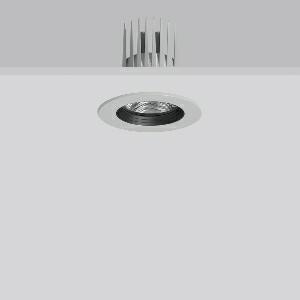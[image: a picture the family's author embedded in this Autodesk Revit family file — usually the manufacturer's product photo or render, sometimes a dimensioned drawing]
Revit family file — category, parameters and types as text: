
# Revit family: heledon_mini_e_901749_004_1_7af7
name_source: partatom
category: Lighting Fixtures
units: mm (PartAtom-declared; Revit-internal decimal feet)

## family parameters
Cut with Voids When Loaded = No
Host = Face
Light Source = No
Part Type = Normal
Room Calculation Point = No
Round Connector Dimension = Use Diameter
Shared = No

## types (1)
- HELEDON mini E (1 x LED Modul 940, 3700 lm, 4000)
    Apparent Load = 29 VA
    Approval mark = CE
    CIE Flux Codes = 99 100 100 100 100
    Color Rendering = 92
    Color Temperature = 4000
    Default Elevation = 1800 mm
    Description = Series: HELEDON mini
Round recessed downlight. Housing: die-cast aluminium, powder-coated. Black plastic ring and recessed LED to prevent glare from the side. Optical assembly with reflector made of MIRO-Silver with 98% total light reflection for outstanding efficiency - can be changed without tools. Best colour rendering index Ra>90. Suitable for Recessed ceiling mounting. Installation without tools thanks to spring fastening system. Including separate LED converter with connecting cable 600 mm.High quality converter without flickering and stroboscopic effect. Through-wiring box (5 pole) available as accessory. The following accessories can be mounted without use of tools: interchangeable lenses, decorative glasses, honeycomb louvre, clear and frosted diffusers, white interchangeable plastic ring. 
Colour: silver
Diameter: 124 mm
Height: 3 mm
Cut-out diameter: 114 mm
Recess height: 170 mm
Luminaire: recess height: 120 mm
Lamp: LED
Socket: without socket
Colour temperature: 4000K
Colour rendering index (CRI): 92
System power: 29 W
Rated luminous flux: 3700 lm
Luminous efficiency: 128 lm/W
Control gear: Regulated power supply
Protection class: II
Type of protection: IP 20
    Height = 0 mm  [stored 0 ft]
    Lamp = 1 x LED Modul 940
    Lamp Light Flux = 3700 lm
    Lamp count = 1
    Length = 124 mm  [stored 0.406824 ft]
    Lifetime = 50000 h
    Luminous efficacy = 128 lm/W
    Manufacturer = RZB
    ModVariant = No
    Model = 901749.004.1
    Mounting Place = Ceiling
    Mounting Type = Recessed
    Number of Poles = 1
    OnlyDefault = Yes
    Power Factor = 1
    Product Name = HELEDON mini E
    Product group = Recessed downlights
    ProductGroupID = 402
    Protection Class = Protection class II
    Protection Degree = IP 20
    RLX_Detail_Level = 1
    RLX_Emergency_Light_Flux = 0 lm
    RLX_Emergency_Type = 0
    RLX_Emergency_Type_DB = No
    RlxData = <blob elided: 127761 chars, md5=bdd58f4d>
    Socket = socket
    Standby Power = 0 W
    System Light Flux = 3700 lm
    System Power = 29 W
    Type Comments = Product without accessories
    Type Image = 901657.004.jpg
    URL = http://relux.com
    VarID = ---
    Voltage = 230 V
    Voltage Range = 220-240 V
    Weight = 0.00 kg
    Width = 0 mm  [stored 0 ft]

note: [stored X ft] marks values corroborated as IEEE doubles in the binary element streams (Revit-internal decimal feet)

## geometry (parser evidence)
native form markers: Blend x4, Sweep x10
no freeform markers — native parametric forms only
